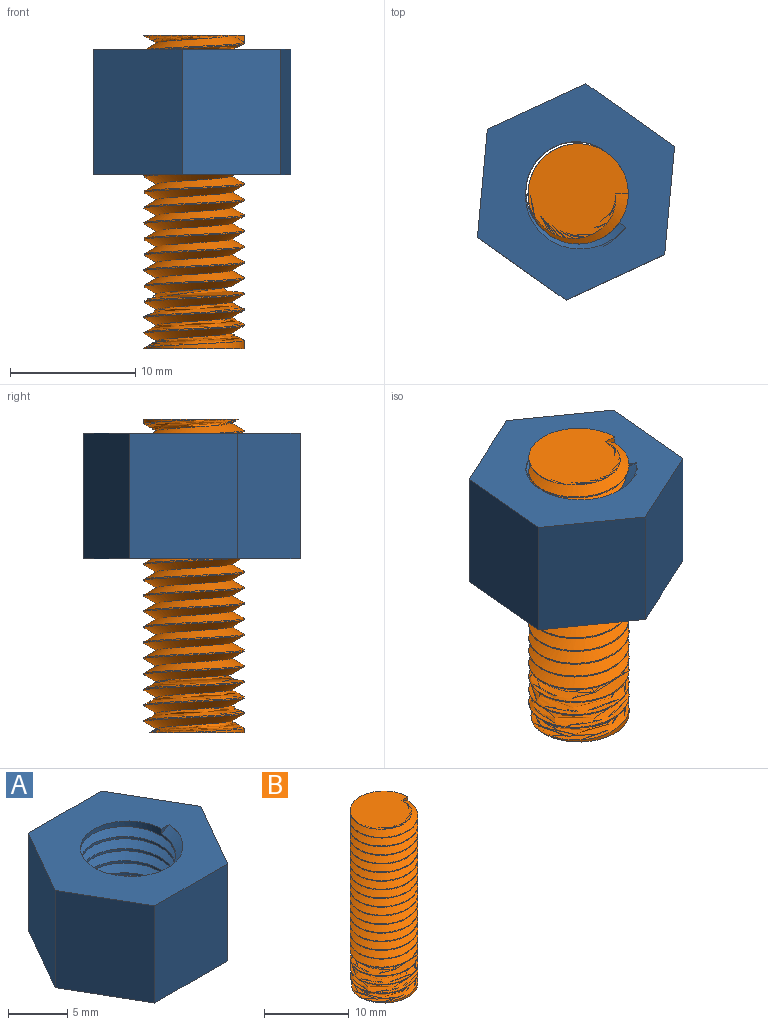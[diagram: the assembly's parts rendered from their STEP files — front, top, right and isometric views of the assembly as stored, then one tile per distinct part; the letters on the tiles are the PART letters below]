
ASSEMBLY  parts=2 mates=1
PART A: 13 faces, bbox 17.9x15.6x11.8 mm
  f0: plane 17.87x15.55mm, normal (0,0,1), area 139.8mm2, adj f1,f2,f3,f4,f5,f6,f7,f9
  f1: plane 10x8.66mm, normal (0,-1,0), area 86.6mm2, adj f0,f2,f6,f8
  f2: plane 10x7.5mm, normal (0.87,-0.5,0), area 86.6mm2, adj f0,f1,f3,f8
  f3: plane 10x7.5mm, normal (0.87,0.5,0), area 86.6mm2, adj f0,f2,f4,f8
  f4: plane 10x8.66mm, normal (0,1,0), area 86.6mm2, adj f0,f3,f5,f8
  f5: plane 10x7.5mm, normal (-0.87,0.5,0), area 86.6mm2, adj f0,f4,f6,f8
  f6: plane 10x7.5mm, normal (-0.87,-0.5,0), area 86.6mm2, adj f0,f1,f5,f8
  f7: cylinder r=4mm len=10mm, axis (0,0,-1), area 50.2mm2, adj f0,f8,f9,f10,f11,f12
  f8: plane 17.88x15.55mm, normal (0,0,-1), area 139.8mm2, adj f1,f2,f3,f4,f5,f6,f7,f10
  f9: bspline ~11.26x10.63mm, area 220.8mm2, adj f0,f7,f10,f11
  f10: bspline ~11.26x10.63mm, area 219.9mm2, adj f7,f8,f9,f12
  f11: plane 0.88x0.51mm, normal (0,1,0), area 0.2mm2, adj f7,f8,f9
  f12: plane 0.88x0.51mm, normal (0,-1,0), area 0.2mm2, adj f0,f7,f10
PART B: 7 faces, bbox 8.9x10.1x27 mm
  f0: cylinder r=4mm len=25mm, axis (0,0,-1), area 113.1mm2, adj f1,f2,f3,f4,f5,f6
  f1: plane 8.77x8.33mm, normal (0,0,1), area 44.9mm2, adj f0,f3,f4
  f2: plane 8.77x8.33mm, normal (0,0,-1), area 44.9mm2, adj f0,f5,f6
  f3: plane 1x0.58mm, normal (0,-1,0), area 0.3mm2, adj f0,f1,f6
  f4: bspline ~25.6x9.33mm, area 503.9mm2, adj f0,f1,f5,f6
  f5: plane 1x0.58mm, normal (0,1,0), area 0.3mm2, adj f0,f2,f4
  f6: bspline ~25.6x9.33mm, area 499.3mm2, adj f0,f2,f3,f4
PLACE A rot(axis=(0,0,-1),35.3deg) t=(-18.82,1.2,12)mm
PLACE B t=(-18.65,1.04,-1.87)mm fixed
MATE cylindrical B.f1 <-> A.f0  axis (0,0,1) through (-18.84,1.32,23.13)mm
